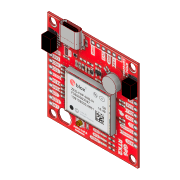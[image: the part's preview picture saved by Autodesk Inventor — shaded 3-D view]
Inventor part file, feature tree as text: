
AUTODESK INVENTOR PART (.ipt)
format: ipt  version: 2018 (Build 220112000, 112)  size: 526,336 bytes
history: native  units: in
note: dims shown in document units (in); Inventor stores cm internally (conversion verified against a paired STEP export)
features: sketch x11, extrude x8, other x4, projected_geometry x3, hole x1, plane x1
ambient origin geometry x8: Origin, YZ Plane, XZ Plane, XY Plane, X Axis, Y Axis, Z Axis, Center Point
bodies: Solid1 (feature_tree)
feature tree (28):
  extrude  "Extrusion1"  Depth=1.7in
  hole  "Hole1"  [1 undecoded]
  plane  "Work Plane1"
  extrude  "Extrusion2"  Depth=0.06in
  extrude  "Extrusion3"  Depth=0.128in
  extrude  "Extrusion4"  Depth=0.05in
  extrude  "Extrusion5"  Depth=0.2in TaperAngle=0.0deg
  extrude  "Extrusion6"  Depth=0.235in
  extrude  "Extrusion7"  Depth=0.121in TaperAngle=0.0deg
  extrude  "Extrusion8"  Depth=0.32in
  other  "Decal1"
  other  "Decal2"
  sketch  "Sketch1"  dims[d0=1.7in d1=1.7in]
  sketch  "Sketch2"  dims[d2=0.03in d3=0.0in d4=0.1in]
  projected_geometry  "Projected Loop1"
  sketch  "Sketch3"  dims[d5=0.132in d6=0.75in d7=0.375in d8=0.25in d9=0.5635in d10=1.0in d11=0.8108in d12=0.06in]
  sketch  "Sketch4"  dims[d13=0.356in d14=0.128in]
  projected_geometry  "Projected Loop2"
  sketch  "Sketch5"  dims[d15=0.322in d16=0.05in]
  projected_geometry  "Projected Loop3"
  sketch  "Sketch6"  dims[d17=0.29in d18=0.0in d19=0.2in d20=0.0in]
  sketch  "Sketch7"  dims[d21=0.167in d22=0.235in]
  sketch  "Sketch8"  dims[d23=0.01in d24=0.121in d25=0.0in]
  sketch  "Sketch9"  dims[d26=0.251in d27=0.32in]
  sketch  "Sketch10"  dims[d28=0.16in]
  other  "Image1"
  sketch  "Sketch11"  dims[d29=0.234in d30=0.121in d31=0.0in d32=0.865in d33=0.67in d34=0.365in d35=0.424in d36=0.102in d37=0.0in d38=0.266in d39=0.512in d40=0.44in d41=0.102in d42=0.0in d43=0.078in d44=0.62in d45=0.21in d46=0.05in d47=0.0in]
  other  "Image2"
note: 1 required parameter value undecoded (feature->parameter linkage not recoverable at this tier; creation-order binding heuristic only, values carry confidence <= 0.55)
